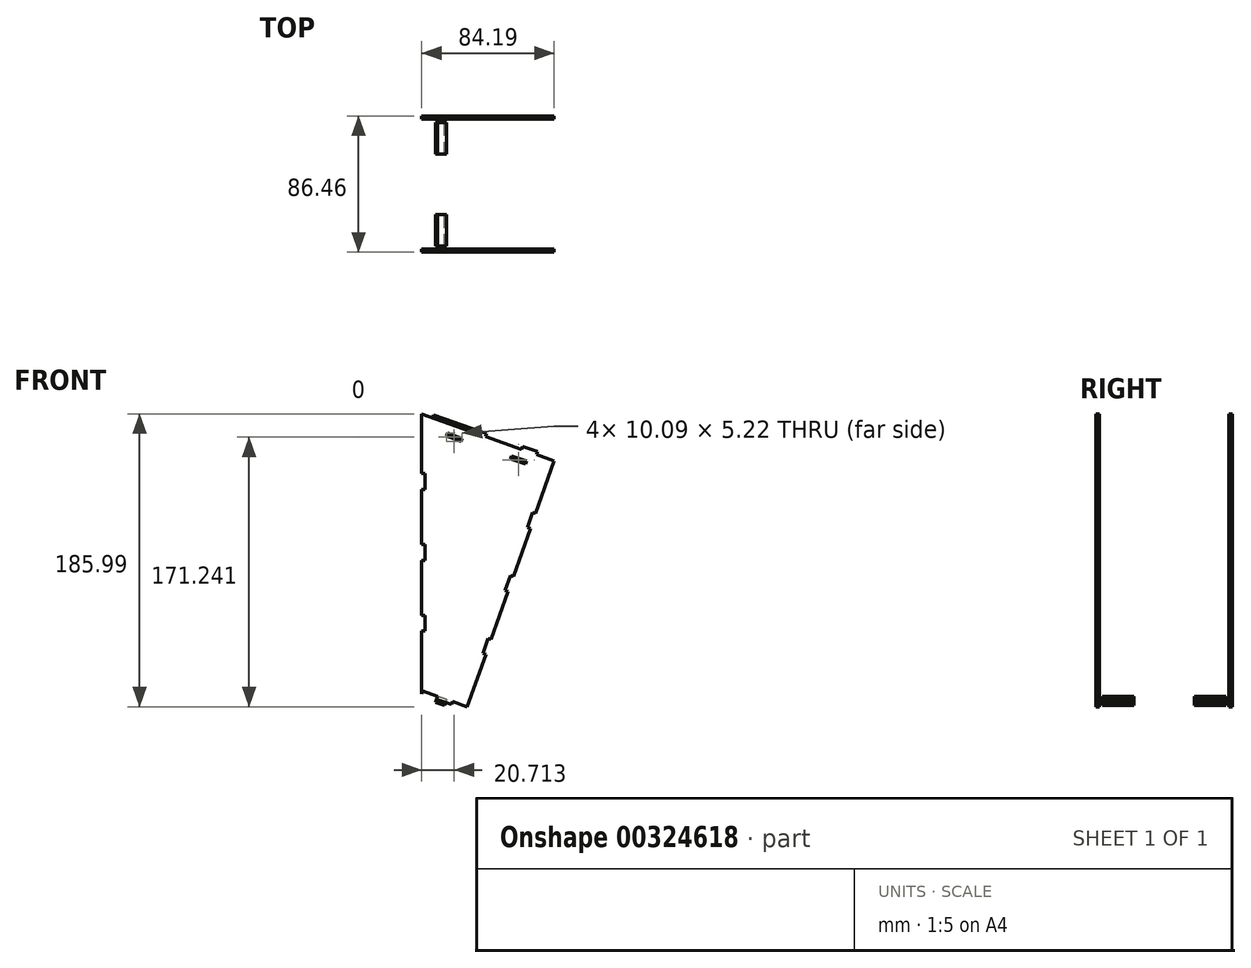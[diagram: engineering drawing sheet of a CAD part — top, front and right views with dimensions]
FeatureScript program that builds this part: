
annotation { "Feature Type Name" : "Feature", "Feature Type Description" : "" }
export const myFeature = defineFeature(function(context is Context, id is Id, definition is map)
    precondition{}
    {
        {
            assignVariable(context, id + "F0", {"name" : "WT", "anyValue" : 2});
        }
        {
            var Q0;
            Q0=qCreatedBy(makeId("Front.planeOp"),FACE);
            var sketch = newSketch(context, id + "F1", { "sketchPlane" : qUnion([Q0])});
            skLineSegment(sketch, "E0", {"start": v(0, 90) * mm, "end": v(0, -90) * mm});
            skLineSegment(sketch, "E1", {"start": v(0, 90) * mm, "end": v(84.85, 60) * mm});
            skLineSegment(sketch, "E2", {"start": v(28.28, -100) * mm, "end": v(0, -90) * mm});
            skLineSegment(sketch, "E3", {"start": v(28.28, -100) * mm, "end": v(84.85, 60) * mm});
            skPoint(sketch, "E4", {"position": v(28.28, 80) * mm});
            skLineSegment(sketch, "E5", {"start": v(14.14, -95) * mm, "end": v(14.14, 85) * mm, "construction": true});
            skLineSegment(sketch, "E6", {"start": v(11.14, -93.94) * mm, "end": v(11.14, -100) * mm});
            skLineSegment(sketch, "E7", {"start": v(11.14, -100) * mm, "end": v(13.14, -100) * mm});
            skLineSegment(sketch, "E8", {"start": v(13.14, -100) * mm, "end": v(13.14, -94.65) * mm});
            skLineSegment(sketch, "E9", {"start": v(15.14, -95.35) * mm, "end": v(15.14, -100) * mm});
            skLineSegment(sketch, "E10", {"start": v(15.14, -100) * mm, "end": v(17.14, -100) * mm});
            skLineSegment(sketch, "E11", {"start": v(17.14, -100) * mm, "end": v(17.14, -96.06) * mm});
            skLineSegment(sketch, "E12", {"start": v(28.28, -100) * mm, "end": v(11.14, -100) * mm, "construction": true});
            skLineSegment(sketch, "E13", {"start": v(11.14, 86.06) * mm, "end": v(11.14, 80) * mm});
            skLineSegment(sketch, "E14", {"start": v(11.14, 80) * mm, "end": v(17.14, 80) * mm});
            skLineSegment(sketch, "E15", {"start": v(17.14, 80) * mm, "end": v(17.14, 83.94) * mm});
            skLineSegment(sketch, "E16", {"start": v(11.14, -93.94) * mm, "end": v(11.14, 80) * mm, "construction": true});
            skLineSegment(sketch, "E17", {"start": v(17.14, -96.06) * mm, "end": v(17.14, 80) * mm, "construction": true});
            skLineSegment(sketch, "E18", {"start": v(0, 79.4) * mm, "end": v(81.52, 50.57) * mm});
            skPoint(sketch, "E19", {"position": v(17.14, 73.33) * mm});
            skSolve(sketch);
        }
        {
            var Q0;
            Q0=qCreatedBy(makeId("Front.planeOp"),FACE);
            var sketch = newSketch(context, id + "F2", { "sketchPlane" : qUnion([Q0])});
            skLineSegment(sketch, "E20.0", {"start": v(0, 90) * mm, "end": v(0, -90) * mm});
            skLineSegment(sketch, "E20.1", {"start": v(0, 90) * mm, "end": v(84.85, 60) * mm});
            skLineSegment(sketch, "E20.2", {"start": v(28.28, -100) * mm, "end": v(84.85, 60) * mm});
            skLineSegment(sketch, "E20.3", {"start": v(28.28, -100) * mm, "end": v(0, -90) * mm});
            skSolve(sketch);
        }
        {
            var Q0;
            Q0=sQuery(id+"F1.wireOp",EDGE,"E18");
            cPlane(context, id + "F3", {"entities" : qUnion([Q0]), "cplaneType" : CPlaneType.LINE_ANGLE, "offset" : 25 * mm, "angle" : 90 * degree, "width" : 150 * mm, "height" : 150 * mm});
        }
        {
            var Q0;
            Q0=qCreatedBy(id+"F3.planeOp",FACE);
            var sketch = newSketch(context, id + "F4", { "sketchPlane" : qUnion([Q0])});
            skLineSegment(sketch, "E21.0", {"start": v(-26.46, 0) * mm, "end": v(60, 0) * mm});
            skLineSegment(sketch, "E22", {"start": v(-26.46, 0) * mm, "end": v(-26.46, -86.46) * mm});
            skLineSegment(sketch, "E23", {"start": v(-26.46, -86.46) * mm, "end": v(60, -86.46) * mm});
            skLineSegment(sketch, "E24", {"start": v(60, -86.46) * mm, "end": v(60, 0) * mm});
            skLineSegment(sketch, "E25.0", {"start": v(48.18, 0) * mm, "end": v(-10.5, 0) * mm, "construction": true});
            skLineSegment(sketch, "E26", {"start": v(-8.28, 0) * mm, "end": v(-8.28, -86.46) * mm, "construction": true});
            skLineSegment(sketch, "E27", {"start": v(-8.28, 0) * mm, "end": v(60, -86.46) * mm, "construction": true});
            skCircle(sketch, "E28", {"center": v(25.86, -43.23) * mm, "radius": 25 * mm});
            skLineSegment(sketch, "E29.0", {"start": v(-24.46, -84.46) * mm, "end": v(62, -84.46) * mm});
            skLineSegment(sketch, "E29.1", {"start": v(-24.46, -2) * mm, "end": v(-24.46, -84.46) * mm});
            skLineSegment(sketch, "E29.2", {"start": v(-24.46, -2) * mm, "end": v(58, -2) * mm});
            skLineSegment(sketch, "E30", {"start": v(-26.46, -43.23) * mm, "end": v(60, -43.23) * mm, "construction": true});
            skLineSegment(sketch, "E31", {"start": v(16.77, -43.23) * mm, "end": v(16.77, 0) * mm, "construction": true});
            skLineSegment(sketch, "E32", {"start": v(16.77, -21.62) * mm, "end": v(-26.46, -21.62) * mm, "construction": true});
            skLineSegment(sketch, "E33", {"start": v(-26.46, -26.62) * mm, "end": v(-24.46, -26.62) * mm});
            skLineSegment(sketch, "E34", {"start": v(-26.46, -16.62) * mm, "end": v(-24.46, -16.62) * mm});
            skLineSegment(sketch, "E35.MirrorCS", {"start": v(-26.46, -59.85) * mm, "end": v(-24.46, -59.85) * mm});
            skLineSegment(sketch, "E36.MirrorCS", {"start": v(-26.46, -69.85) * mm, "end": v(-24.46, -69.85) * mm});
            skLineSegment(sketch, "E37", {"start": v(-4.85, -21.62) * mm, "end": v(-4.85, -86.46) * mm, "construction": true});
            skLineSegment(sketch, "E38", {"start": v(-9.85, -86.46) * mm, "end": v(-9.85, -84.46) * mm});
            skLineSegment(sketch, "E39", {"start": v(0.15, -86.46) * mm, "end": v(0.15, -84.46) * mm});
            skLineSegment(sketch, "E40.MirrorCS", {"start": v(0.15, 0) * mm, "end": v(0.15, -2) * mm});
            skLineSegment(sketch, "E41.MirrorCS", {"start": v(-9.85, 0) * mm, "end": v(-9.85, -2) * mm});
            skLineSegment(sketch, "E42.MirrorCS", {"start": v(33.38, -86.46) * mm, "end": v(33.38, -84.46) * mm});
            skLineSegment(sketch, "E43.MirrorCS", {"start": v(43.38, -86.46) * mm, "end": v(43.38, -84.46) * mm});
            skLineSegment(sketch, "E44.MirrorCS", {"start": v(33.38, 0) * mm, "end": v(33.38, -2) * mm});
            skLineSegment(sketch, "E45.MirrorCS", {"start": v(43.38, 0) * mm, "end": v(43.38, -2) * mm});
            skLineSegment(sketch, "E46.MirrorCS", {"start": v(60, -69.85) * mm, "end": v(58, -69.85) * mm});
            skLineSegment(sketch, "E47.MirrorCS", {"start": v(60, -59.85) * mm, "end": v(58, -59.85) * mm});
            skLineSegment(sketch, "E48.MirrorCS", {"start": v(60, -26.62) * mm, "end": v(58, -26.62) * mm});
            skLineSegment(sketch, "E49.MirrorCS", {"start": v(60, -16.62) * mm, "end": v(58, -16.62) * mm});
            skLineSegment(sketch, "E50", {"start": v(60, -84.46) * mm, "end": v(62, -84.46) * mm});
            skLineSegment(sketch, "E51", {"start": v(58, -2) * mm, "end": v(60, -2) * mm});
            skLineSegment(sketch, "E52", {"start": v(58, 0) * mm, "end": v(58, -86.46) * mm});
            skSolve(sketch);
        }
        {
            var Q0;
            Q0=sQuery(id+"F2.wireOp",EDGE,"E20.1");
            cPlane(context, id + "F5", {"entities" : qUnion([Q0]), "cplaneType" : CPlaneType.LINE_ANGLE, "offset" : 25 * mm, "angle" : 90 * degree, "width" : 150 * mm, "height" : 150 * mm});
        }
        {
            var Q0;
            Q0=qCreatedBy(id+"F5.planeOp",FACE);
            var sketch = newSketch(context, id + "F6", { "sketchPlane" : qUnion([Q0])});
            skLineSegment(sketch, "E53.0", {"start": v(-30, 0) * mm, "end": v(60, 0) * mm});
            skLineSegment(sketch, "E54.0", {"start": v(60, -86.46) * mm, "end": v(60, 0) * mm});
            skLineSegment(sketch, "E55.0", {"start": v(-8.28, 0) * mm, "end": v(60, -86.46) * mm, "construction": true});
            skCircle(sketch, "E56", {"center": v(25.86, -43.23) * mm, "radius": 30 * mm});
            skLineSegment(sketch, "E57", {"start": v(-30, 0) * mm, "end": v(-30, -86.46) * mm});
            skLineSegment(sketch, "E58.0", {"start": v(-18.18, 0) * mm, "end": v(-16.16, 0) * mm});
            skLineSegment(sketch, "E59.0", {"start": v(-10.5, 0) * mm, "end": v(-11.82, 0) * mm});
            skLineSegment(sketch, "E60", {"start": v(-22, 0) * mm, "end": v(-22, -95.78) * mm});
            skLineSegment(sketch, "E61", {"start": v(-12, 0) * mm, "end": v(-12, -95.78) * mm});
            skLineSegment(sketch, "E62", {"start": v(-22, -2) * mm, "end": v(-12, -2) * mm});
            skLineSegment(sketch, "E63", {"start": v(-22, -84.46) * mm, "end": v(-12, -84.46) * mm});
            skLineSegment(sketch, "E64", {"start": v(-30, -86.46) * mm, "end": v(60, -86.46) * mm});
            skLineSegment(sketch, "E65", {"start": v(-12, -84.46) * mm, "end": v(60, -84.46) * mm});
            skLineSegment(sketch, "E66", {"start": v(-22, -84.46) * mm, "end": v(-30, -84.46) * mm});
            skLineSegment(sketch, "E67", {"start": v(-28, -84.46) * mm, "end": v(-28, -2) * mm});
            skLineSegment(sketch, "E68", {"start": v(-22, -2) * mm, "end": v(-30, -2) * mm});
            skLineSegment(sketch, "E69", {"start": v(-12, -2) * mm, "end": v(60, -2) * mm});
            skLineSegment(sketch, "E70", {"start": v(25.86, -43.23) * mm, "end": v(25.86, 0) * mm, "construction": true});
            skLineSegment(sketch, "E71", {"start": v(25.86, 0) * mm, "end": v(60, -2) * mm, "construction": true});
            skLineSegment(sketch, "E72", {"start": v(42.93, -1) * mm, "end": v(42.93, 0) * mm, "construction": true});
            skLineSegment(sketch, "E73", {"start": v(37.93, 0) * mm, "end": v(37.93, -2) * mm});
            skLineSegment(sketch, "E74", {"start": v(47.93, -2) * mm, "end": v(47.93, 0) * mm});
            skLineSegment(sketch, "E75.MirrorCS", {"start": v(13.79, 0) * mm, "end": v(13.79, -2) * mm});
            skLineSegment(sketch, "E76.MirrorCS", {"start": v(3.79, -2) * mm, "end": v(3.79, 0) * mm});
            skLineSegment(sketch, "E77", {"start": v(25.86, -43.23) * mm, "end": v(44.36, -43.23) * mm, "construction": true});
            skLineSegment(sketch, "E78.MirrorCS", {"start": v(3.79, -84.46) * mm, "end": v(3.79, -86.46) * mm});
            skLineSegment(sketch, "E79.MirrorCS", {"start": v(13.79, -86.46) * mm, "end": v(13.79, -84.46) * mm});
            skLineSegment(sketch, "E80.MirrorCS", {"start": v(37.93, -86.46) * mm, "end": v(37.93, -84.46) * mm});
            skLineSegment(sketch, "E81.MirrorCS", {"start": v(47.93, -84.46) * mm, "end": v(47.93, -86.46) * mm});
            skSolve(sketch);
        }
        {
            var Q0;
            Q0=sQuery(id+"F1.wireOp",EDGE,"E1");
            cPlane(context, id + "F7", {"entities" : qUnion([Q0]), "cplaneType" : CPlaneType.LINE_ANGLE, "offset" : 25 * mm, "angle" : 90 * degree, "width" : 150 * mm, "height" : 150 * mm});
        }
        {
            var Q0;
            Q0=qCreatedBy(makeId("Right.planeOp"),FACE);
            var sketch = newSketch(context, id + "F8", { "sketchPlane" : qUnion([Q0])});
            skLineSegment(sketch, "E82.0", {"start": v(0, 90) * mm, "end": v(0, -90) * mm});
            skLineSegment(sketch, "E83", {"start": v(-86.46, 90) * mm, "end": v(-86.46, -90) * mm});
            skLineSegment(sketch, "E84", {"start": v(-86.46, -90) * mm, "end": v(0, -90) * mm});
            skLineSegment(sketch, "E85.0", {"start": v(0, 90) * mm, "end": v(-86.46, 90) * mm});
            skLineSegment(sketch, "E86.0", {"start": v(-2, 88) * mm, "end": v(-2, -88) * mm});
            skLineSegment(sketch, "E86.1", {"start": v(-2, 88) * mm, "end": v(-84.46, 88) * mm});
            skLineSegment(sketch, "E86.2", {"start": v(-84.46, 88) * mm, "end": v(-84.46, -88) * mm});
            skLineSegment(sketch, "E86.3", {"start": v(-84.46, -88) * mm, "end": v(-2, -88) * mm});
            skLineSegment(sketch, "E87", {"start": v(-43.23, 90) * mm, "end": v(-43.23, -90) * mm, "construction": true});
            skLineSegment(sketch, "E88", {"start": v(-86.46, 0) * mm, "end": v(0, 0) * mm, "construction": true});
            skLineSegment(sketch, "E89", {"start": v(-86.46, 90) * mm, "end": v(0, -90) * mm, "construction": true});
            skLineSegment(sketch, "E90", {"start": v(-43.23, 0) * mm, "end": v(-86.46, -90) * mm, "construction": true});
            skLineSegment(sketch, "E91", {"start": v(-64.85, -45) * mm, "end": v(0, -45) * mm, "construction": true});
            skLineSegment(sketch, "E92", {"start": v(0, -40) * mm, "end": v(-2, -40) * mm});
            skLineSegment(sketch, "E93.MirrorCS", {"start": v(0, -50) * mm, "end": v(-2, -50) * mm});
            skLineSegment(sketch, "E94", {"start": v(-21.62, -22.5) * mm, "end": v(0, -22.5) * mm, "construction": true});
            skLineSegment(sketch, "E95.MirrorCS", {"start": v(0, -5) * mm, "end": v(-2, -5) * mm});
            skLineSegment(sketch, "E96.MirrorCS", {"start": v(0, 5) * mm, "end": v(-2, 5) * mm});
            skLineSegment(sketch, "E97", {"start": v(0, -45) * mm, "end": v(-43.23, 0) * mm, "construction": true});
            skLineSegment(sketch, "E98.MirrorCS", {"start": v(0, 40) * mm, "end": v(-2, 40) * mm});
            skLineSegment(sketch, "E99.MirrorCS", {"start": v(0, 50) * mm, "end": v(-2, 50) * mm});
            skLineSegment(sketch, "E100.MirrorCS", {"start": v(-86.46, 50) * mm, "end": v(-84.46, 50) * mm});
            skLineSegment(sketch, "E101.MirrorCS", {"start": v(-86.46, 40) * mm, "end": v(-84.46, 40) * mm});
            skLineSegment(sketch, "E102.MirrorCS", {"start": v(-86.46, 5) * mm, "end": v(-84.46, 5) * mm});
            skLineSegment(sketch, "E103.MirrorCS", {"start": v(-86.46, -5) * mm, "end": v(-84.46, -5) * mm});
            skLineSegment(sketch, "E104.MirrorCS", {"start": v(-86.46, -40) * mm, "end": v(-84.46, -40) * mm});
            skLineSegment(sketch, "E105.MirrorCS", {"start": v(-86.46, -50) * mm, "end": v(-84.46, -50) * mm});
            skLineSegment(sketch, "E106", {"start": v(-21.62, -22.5) * mm, "end": v(-21.62, -90) * mm, "construction": true});
            skLineSegment(sketch, "E107", {"start": v(-16.62, -88) * mm, "end": v(-16.62, -90) * mm});
            skLineSegment(sketch, "E108.MirrorCS", {"start": v(-26.62, -88) * mm, "end": v(-26.62, -90) * mm});
            skLineSegment(sketch, "E109.MirrorCS", {"start": v(-59.85, -88) * mm, "end": v(-59.85, -90) * mm});
            skLineSegment(sketch, "E110.MirrorCS", {"start": v(-69.85, -88) * mm, "end": v(-69.85, -90) * mm});
            skLineSegment(sketch, "E111.MirrorCS", {"start": v(-16.62, 88) * mm, "end": v(-16.62, 90) * mm});
            skLineSegment(sketch, "E112.MirrorCS", {"start": v(-26.62, 88) * mm, "end": v(-26.62, 90) * mm});
            skLineSegment(sketch, "E113.MirrorCS", {"start": v(-59.85, 88) * mm, "end": v(-59.85, 90) * mm});
            skLineSegment(sketch, "E114.MirrorCS", {"start": v(-69.85, 88) * mm, "end": v(-69.85, 90) * mm});
            skSolve(sketch);
        }
        {
            var Q0;
            Q0=sQuery(id+"F1.wireOp",EDGE,"E2");
            cPlane(context, id + "F9", {"entities" : qUnion([Q0]), "cplaneType" : CPlaneType.LINE_ANGLE, "offset" : 25 * mm, "angle" : 90 * degree, "width" : 150 * mm, "height" : 150 * mm});
        }
        {
            var Q0;
            Q0=sQuery(id+"F1.wireOp",EDGE,"E3");
            cPlane(context, id + "F10", {"entities" : qUnion([Q0]), "cplaneType" : CPlaneType.LINE_ANGLE, "offset" : 25 * mm, "angle" : 0 * degree, "width" : 150 * mm, "height" : 150 * mm});
        }
        {
            var Q0;
            Q0=qCreatedBy(id+"F10.planeOp",FACE);
            var sketch = newSketch(context, id + "F11", { "sketchPlane" : qUnion([Q0])});
            skLineSegment(sketch, "E115.0", {"start": v(0, -84.85) * mm, "end": v(0, 84.85) * mm});
            skLineSegment(sketch, "E116.0", {"start": v(-86.46, 84.85) * mm, "end": v(0, 84.85) * mm});
            skLineSegment(sketch, "E117", {"start": v(-86.46, 84.85) * mm, "end": v(-86.46, -84.85) * mm});
            skLineSegment(sketch, "E118", {"start": v(-86.46, -84.85) * mm, "end": v(0, -84.85) * mm});
            skLineSegment(sketch, "E119.0", {"start": v(-84.46, 82.85) * mm, "end": v(-84.46, -82.85) * mm});
            skLineSegment(sketch, "E119.1", {"start": v(-84.46, 82.85) * mm, "end": v(-2, 82.85) * mm});
            skLineSegment(sketch, "E119.2", {"start": v(-2, -82.85) * mm, "end": v(-2, 82.85) * mm});
            skLineSegment(sketch, "E119.3", {"start": v(-84.46, -82.85) * mm, "end": v(-2, -82.85) * mm});
            skLineSegment(sketch, "E120", {"start": v(-43.23, 84.85) * mm, "end": v(-43.23, -84.85) * mm, "construction": true});
            skLineSegment(sketch, "E121", {"start": v(0, 0) * mm, "end": v(-86.46, 0) * mm, "construction": true});
            skLineSegment(sketch, "E122", {"start": v(-86.46, 0) * mm, "end": v(-43.23, 84.85) * mm, "construction": true});
            skLineSegment(sketch, "E123", {"start": v(-64.85, 42.43) * mm, "end": v(-64.85, 84.85) * mm, "construction": true});
            skLineSegment(sketch, "E124", {"start": v(-69.85, 82.85) * mm, "end": v(-69.85, 84.85) * mm});
            skLineSegment(sketch, "E125", {"start": v(-59.85, 82.85) * mm, "end": v(-59.85, 84.85) * mm});
            skLineSegment(sketch, "E126.MirrorCS", {"start": v(-16.62, 82.85) * mm, "end": v(-16.62, 84.85) * mm});
            skLineSegment(sketch, "E127.MirrorCS", {"start": v(-26.62, 82.85) * mm, "end": v(-26.62, 84.85) * mm});
            skLineSegment(sketch, "E128.MirrorCS", {"start": v(-69.85, -82.85) * mm, "end": v(-69.85, -84.85) * mm});
            skLineSegment(sketch, "E129.MirrorCS", {"start": v(-59.85, -82.85) * mm, "end": v(-59.85, -84.85) * mm});
            skLineSegment(sketch, "E130.MirrorCS", {"start": v(-26.62, -82.85) * mm, "end": v(-26.62, -84.85) * mm});
            skLineSegment(sketch, "E131.MirrorCS", {"start": v(-16.62, -82.85) * mm, "end": v(-16.62, -84.85) * mm});
            skLineSegment(sketch, "E132", {"start": v(-86.46, 5) * mm, "end": v(-84.46, 5) * mm});
            skLineSegment(sketch, "E133", {"start": v(-86.46, -5) * mm, "end": v(-84.46, -5) * mm});
            skLineSegment(sketch, "E134", {"start": v(-64.85, 42.43) * mm, "end": v(-86.46, 42.43) * mm, "construction": true});
            skLineSegment(sketch, "E135", {"start": v(-86.46, 47.43) * mm, "end": v(-84.46, 47.43) * mm});
            skLineSegment(sketch, "E136", {"start": v(-86.46, 37.43) * mm, "end": v(-84.46, 37.43) * mm});
            skLineSegment(sketch, "E137.MirrorCS", {"start": v(0, 47.43) * mm, "end": v(-2, 47.43) * mm});
            skLineSegment(sketch, "E138.MirrorCS", {"start": v(0, 37.43) * mm, "end": v(-2, 37.43) * mm});
            skLineSegment(sketch, "E139.MirrorCS", {"start": v(0, 5) * mm, "end": v(-2, 5) * mm});
            skLineSegment(sketch, "E140.MirrorCS", {"start": v(0, -5) * mm, "end": v(-2, -5) * mm});
            skLineSegment(sketch, "E141.MirrorCS", {"start": v(-86.46, -37.43) * mm, "end": v(-84.46, -37.43) * mm});
            skLineSegment(sketch, "E142.MirrorCS", {"start": v(-86.46, -47.43) * mm, "end": v(-84.46, -47.43) * mm});
            skLineSegment(sketch, "E143.MirrorCS", {"start": v(0, -37.43) * mm, "end": v(-2, -37.43) * mm});
            skLineSegment(sketch, "E144.MirrorCS", {"start": v(0, -47.43) * mm, "end": v(-2, -47.43) * mm});
            skSolve(sketch);
        }
        {
            var Q0;
            Q0=sQuery(id+"F11.wireOp",EDGE,"E117");
            cPlane(context, id + "F12", {"entities" : qUnion([Q0]), "cplaneType" : CPlaneType.LINE_ANGLE, "offset" : 25 * mm, "angle" : 90 * degree, "width" : 150 * mm, "height" : 150 * mm});
        }
        {
            var Q0;
            Q0=qCreatedBy(id+"F12.planeOp",FACE);
            var sketch = newSketch(context, id + "F13", { "sketchPlane" : qUnion([Q0])});
            skLineSegment(sketch, "E145.0", {"start": v(0, 90) * mm, "end": v(0, -90) * mm});
            skLineSegment(sketch, "E145.1", {"start": v(-28.28, -100) * mm, "end": v(0, -90) * mm});
            skLineSegment(sketch, "E145.2", {"start": v(-28.28, -100) * mm, "end": v(-84.85, 60) * mm});
            skLineSegment(sketch, "E145.3", {"start": v(0, 90) * mm, "end": v(-84.85, 60) * mm});
            skSolve(sketch);
        }
        {
            var Q0;
            Q0=qCreatedBy(id+"F9.planeOp",FACE);
            var sketch = newSketch(context, id + "F14", { "sketchPlane" : qUnion([Q0])});
            skLineSegment(sketch, "E146.0", {"start": v(60, -86.46) * mm, "end": v(60, 0) * mm});
            skLineSegment(sketch, "E147.0", {"start": v(60, -86.46) * mm, "end": v(30, -86.46) * mm});
            skLineSegment(sketch, "E148", {"start": v(30, -86.46) * mm, "end": v(30, 0) * mm});
            skLineSegment(sketch, "E149", {"start": v(30, 0) * mm, "end": v(60, 0) * mm});
            skLineSegment(sketch, "E150.0", {"start": v(32, -84.46) * mm, "end": v(32, -2) * mm});
            skLineSegment(sketch, "E150.1", {"start": v(58, -84.46) * mm, "end": v(32, -84.46) * mm});
            skLineSegment(sketch, "E150.2", {"start": v(58, -84.46) * mm, "end": v(58, -2) * mm});
            skLineSegment(sketch, "E150.3", {"start": v(32, -2) * mm, "end": v(58, -2) * mm});
            skLineSegment(sketch, "E151", {"start": v(58, -84.46) * mm, "end": v(32, -2) * mm, "construction": true});
            skLineSegment(sketch, "E152", {"start": v(45, -43.23) * mm, "end": v(32, -43.23) * mm, "construction": true});
            skLineSegment(sketch, "E153.bottom", {"start": v(48, -84.46) * mm, "end": v(38, -84.46) * mm});
            skLineSegment(sketch, "E153.top", {"start": v(48, -2) * mm, "end": v(38, -2) * mm});
            skLineSegment(sketch, "E153.left", {"start": v(48, -84.46) * mm, "end": v(48, -2) * mm});
            skLineSegment(sketch, "E153.right", {"start": v(38, -84.46) * mm, "end": v(38, -2) * mm});
            skPoint(sketch, "E153.middle", {"position": v(43, -43.23) * mm});
            skLineSegment(sketch, "E154.0", {"start": v(46, -82.46) * mm, "end": v(46, -4) * mm});
            skLineSegment(sketch, "E154.1", {"start": v(46, -82.46) * mm, "end": v(40, -82.46) * mm});
            skLineSegment(sketch, "E154.2", {"start": v(40, -82.46) * mm, "end": v(40, -4) * mm});
            skLineSegment(sketch, "E154.3", {"start": v(46, -4) * mm, "end": v(40, -4) * mm});
            skLineSegment(sketch, "E155", {"start": v(45, 0) * mm, "end": v(45, -2) * mm, "construction": true});
            skLineSegment(sketch, "E156", {"start": v(40, 0) * mm, "end": v(40, -2) * mm});
            skLineSegment(sketch, "E157.MirrorCS", {"start": v(50, 0) * mm, "end": v(50, -2) * mm});
            skLineSegment(sketch, "E158.MirrorCS", {"start": v(40, -86.46) * mm, "end": v(40, -84.46) * mm});
            skLineSegment(sketch, "E159.MirrorCS", {"start": v(50, -86.46) * mm, "end": v(50, -84.46) * mm});
            skLineSegment(sketch, "E160", {"start": v(40, -24) * mm, "end": v(46, -24) * mm});
            skLineSegment(sketch, "E161.MirrorCS", {"start": v(40, -62.46) * mm, "end": v(46, -62.46) * mm});
            skSolve(sketch);
        }
        {
            var Q0;
            Q0=makeQuery(id+"F2.imprint","IMPRINT",FACE,{"disambiguationData":[TD([[makeQuery(id+"F2.imprint","IMPRINT",EDGE,{"derivedFrom":sQuery(id+"F2.wireOp",EDGE,"E20.0")}),1.0]])]});
            extrude(context, id + "F15", {"entities" : qUnion([Q0]), "depth" : (getVariable(context, 'WT')) * mm});
        }
        {
            var Q0;
            {var subQ12=sQuery(id+"F8.wireOp",EDGE,"E86.1");var subQ16=sQuery(id+"F8.wireOp",EDGE,"E86.0");var subQ21=makeQuery(id+"F8.imprint","INTERSECT",VERTEX,{"derivedFrom":[subQ16,subQ12]});Q0=makeQuery(id+"F8.imprint","IMPRINT",FACE,{"disambiguationData":[TD([[makeQuery(id+"F8.imprint","IMPRINT",EDGE,{"disambiguationData":[TD([[subQ21,-1.0]])],"derivedFrom":subQ16}),-1.0]])]});}
            var Q1;
            {var subQ0=sQuery(id+"F8.wireOp",EDGE,"E98.MirrorCS");Q1=makeQuery(id+"F8.imprint","IMPRINT",FACE,{"disambiguationData":[TD([[makeQuery(id+"F8.imprint","IMPRINT",EDGE,{"derivedFrom":subQ0}),-1.0]])]});}
            var Q2;
            {var subQ0=sQuery(id+"F8.wireOp",EDGE,"E100.MirrorCS");Q2=makeQuery(id+"F8.imprint","IMPRINT",FACE,{"disambiguationData":[TD([[makeQuery(id+"F8.imprint","IMPRINT",EDGE,{"derivedFrom":subQ0}),-1.0]])]});}
            var Q3;
            {var subQ0=sQuery(id+"F8.wireOp",EDGE,"E102.MirrorCS");Q3=makeQuery(id+"F8.imprint","IMPRINT",FACE,{"disambiguationData":[TD([[makeQuery(id+"F8.imprint","IMPRINT",EDGE,{"derivedFrom":subQ0}),-1.0]])]});}
            var Q4;
            {var subQ0=sQuery(id+"F8.wireOp",EDGE,"E104.MirrorCS");Q4=makeQuery(id+"F8.imprint","IMPRINT",FACE,{"disambiguationData":[TD([[makeQuery(id+"F8.imprint","IMPRINT",EDGE,{"derivedFrom":subQ0}),-1.0]])]});}
            var Q5;
            {var subQ0=sQuery(id+"F8.wireOp",EDGE,"E109.MirrorCS");Q5=makeQuery(id+"F8.imprint","IMPRINT",FACE,{"disambiguationData":[TD([[makeQuery(id+"F8.imprint","IMPRINT",EDGE,{"derivedFrom":subQ0}),-1.0]])]});}
            var Q6;
            {var subQ0=sQuery(id+"F8.wireOp",EDGE,"E107");Q6=makeQuery(id+"F8.imprint","IMPRINT",FACE,{"disambiguationData":[TD([[makeQuery(id+"F8.imprint","IMPRINT",EDGE,{"derivedFrom":subQ0}),-1.0]])]});}
            var Q7;
            {var subQ0=sQuery(id+"F8.wireOp",EDGE,"E92");Q7=makeQuery(id+"F8.imprint","IMPRINT",FACE,{"disambiguationData":[TD([[makeQuery(id+"F8.imprint","IMPRINT",EDGE,{"derivedFrom":subQ0}),1.0]])]});}
            var Q8;
            {var subQ0=sQuery(id+"F8.wireOp",EDGE,"E95.MirrorCS");Q8=makeQuery(id+"F8.imprint","IMPRINT",FACE,{"disambiguationData":[TD([[makeQuery(id+"F8.imprint","IMPRINT",EDGE,{"derivedFrom":subQ0}),-1.0]])]});}
            extrude(context, id + "F16", {"entities" : qUnion([Q0, Q1, Q2, Q3, Q4, Q5, Q6, Q7, Q8]), "depth" : (getVariable(context, 'WT')) * mm});
        }
        {
            var Q0;
            {var subQ4=sQuery(id+"F11.wireOp",EDGE,"E119.0");var subQ7=sQuery(id+"F11.wireOp",EDGE,"E119.1");var subQ22=makeQuery(id+"F11.imprint","INTERSECT",VERTEX,{"derivedFrom":[subQ4,subQ7]});Q0=makeQuery(id+"F11.imprint","IMPRINT",FACE,{"disambiguationData":[TD([[makeQuery(id+"F11.imprint","IMPRINT",EDGE,{"disambiguationData":[TD([[subQ22,-1.0]])],"derivedFrom":subQ4}),1.0]])]});}
            var Q1;
            {var subQ0=sQuery(id+"F11.wireOp",EDGE,"E132");Q1=makeQuery(id+"F11.imprint","IMPRINT",FACE,{"disambiguationData":[TD([[makeQuery(id+"F11.imprint","IMPRINT",EDGE,{"derivedFrom":subQ0}),-1.0]])]});}
            var Q2;
            {var subQ0=sQuery(id+"F11.wireOp",EDGE,"E135");Q2=makeQuery(id+"F11.imprint","IMPRINT",FACE,{"disambiguationData":[TD([[makeQuery(id+"F11.imprint","IMPRINT",EDGE,{"derivedFrom":subQ0}),-1.0]])]});}
            var Q3;
            {var subQ0=sQuery(id+"F11.wireOp",EDGE,"E141.MirrorCS");Q3=makeQuery(id+"F11.imprint","IMPRINT",FACE,{"disambiguationData":[TD([[makeQuery(id+"F11.imprint","IMPRINT",EDGE,{"derivedFrom":subQ0}),-1.0]])]});}
            var Q4;
            {var subQ0=sQuery(id+"F11.wireOp",EDGE,"E128.MirrorCS");Q4=makeQuery(id+"F11.imprint","IMPRINT",FACE,{"disambiguationData":[TD([[makeQuery(id+"F11.imprint","IMPRINT",EDGE,{"derivedFrom":subQ0}),1.0]])]});}
            var Q5;
            {var subQ0=sQuery(id+"F11.wireOp",EDGE,"E130.MirrorCS");Q5=makeQuery(id+"F11.imprint","IMPRINT",FACE,{"disambiguationData":[TD([[makeQuery(id+"F11.imprint","IMPRINT",EDGE,{"derivedFrom":subQ0}),1.0]])]});}
            var Q6;
            {var subQ0=sQuery(id+"F11.wireOp",EDGE,"E143.MirrorCS");Q6=makeQuery(id+"F11.imprint","IMPRINT",FACE,{"disambiguationData":[TD([[makeQuery(id+"F11.imprint","IMPRINT",EDGE,{"derivedFrom":subQ0}),1.0]])]});}
            var Q7;
            {var subQ0=sQuery(id+"F11.wireOp",EDGE,"E139.MirrorCS");Q7=makeQuery(id+"F11.imprint","IMPRINT",FACE,{"disambiguationData":[TD([[makeQuery(id+"F11.imprint","IMPRINT",EDGE,{"derivedFrom":subQ0}),1.0]])]});}
            var Q8;
            {var subQ0=sQuery(id+"F11.wireOp",EDGE,"E137.MirrorCS");Q8=makeQuery(id+"F11.imprint","IMPRINT",FACE,{"disambiguationData":[TD([[makeQuery(id+"F11.imprint","IMPRINT",EDGE,{"derivedFrom":subQ0}),1.0]])]});}
            var Q9;
            {var subQ0=sQuery(id+"F11.wireOp",EDGE,"E126.MirrorCS");Q9=makeQuery(id+"F11.imprint","IMPRINT",FACE,{"disambiguationData":[TD([[makeQuery(id+"F11.imprint","IMPRINT",EDGE,{"derivedFrom":subQ0}),1.0]])]});}
            var Q10;
            {var subQ0=sQuery(id+"F11.wireOp",EDGE,"E124");Q10=makeQuery(id+"F11.imprint","IMPRINT",FACE,{"disambiguationData":[TD([[makeQuery(id+"F11.imprint","IMPRINT",EDGE,{"derivedFrom":subQ0}),-1.0]])]});}
            extrude(context, id + "F17", {"entities" : qUnion([Q0, Q1, Q2, Q3, Q4, Q5, Q6, Q7, Q8, Q9, Q10]), "oppositeDirection" : true, "depth" : (getVariable(context, 'WT')) * mm});
        }
        {
            var Q0;
            Q0=makeQuery(id+"F6.imprint","IMPRINT",FACE,{"disambiguationData":[TD([[makeQuery(id+"F6.imprint","IMPRINT",EDGE,{"derivedFrom":sQuery(id+"F6.wireOp",EDGE,"E56")}),-1.0]])]});
            var Q1;
            {var subQ5=sQuery(id+"F6.wireOp",EDGE,"E67");Q1=makeQuery(id+"F6.imprint","IMPRINT",FACE,{"disambiguationData":[TD([[makeQuery(id+"F6.imprint","IMPRINT",EDGE,{"derivedFrom":subQ5}),1.0]])]});}
            var Q2;
            {var subQ4=sQuery(id+"F6.wireOp",EDGE,"E64");var subQ5=sQuery(id+"F6.wireOp",EDGE,"E57");var subQ6=makeQuery(id+"F6.imprint","INTERSECT",VERTEX,{"derivedFrom":[subQ5,subQ4]});Q2=makeQuery(id+"F6.imprint","IMPRINT",FACE,{"disambiguationData":[TD([[makeQuery(id+"F6.imprint","IMPRINT",EDGE,{"disambiguationData":[TD([[subQ6,1.0]])],"derivedFrom":subQ5}),1.0]])]});}
            var Q3;
            {var subQ3=sQuery(id+"F6.wireOp",EDGE,"E63");Q3=makeQuery(id+"F6.imprint","IMPRINT",FACE,{"disambiguationData":[TD([[makeQuery(id+"F6.imprint","IMPRINT",EDGE,{"derivedFrom":subQ3}),-1.0]])]});}
            var Q4;
            {var subQ5=sQuery(id+"F6.wireOp",EDGE,"E78.MirrorCS");Q4=makeQuery(id+"F6.imprint","IMPRINT",FACE,{"disambiguationData":[TD([[makeQuery(id+"F6.imprint","IMPRINT",EDGE,{"derivedFrom":subQ5}),-1.0]])]});}
            var Q5;
            {var subQ0=sQuery(id+"F6.wireOp",EDGE,"E79.MirrorCS");Q5=makeQuery(id+"F6.imprint","IMPRINT",FACE,{"disambiguationData":[TD([[makeQuery(id+"F6.imprint","IMPRINT",EDGE,{"derivedFrom":subQ0}),-1.0]])]});}
            var Q6;
            {var subQ5=sQuery(id+"F6.wireOp",EDGE,"E81.MirrorCS");Q6=makeQuery(id+"F6.imprint","IMPRINT",FACE,{"disambiguationData":[TD([[makeQuery(id+"F6.imprint","IMPRINT",EDGE,{"derivedFrom":subQ5}),1.0]])]});}
            var Q7;
            {var subQ0=sQuery(id+"F6.wireOp",EDGE,"2n5WLC9Z-0obv-Y2U2-hiql-T8fxuz6A8fkv");Q7=makeQuery(id+"F6.imprint","IMPRINT",FACE,{"disambiguationData":[TD([[makeQuery(id+"F6.imprint","IMPRINT",EDGE,{"derivedFrom":subQ0}),-1.0]])]});}
            var Q8;
            {var subQ3=sQuery(id+"F6.wireOp",EDGE,"E74");Q8=makeQuery(id+"F6.imprint","IMPRINT",FACE,{"disambiguationData":[TD([[makeQuery(id+"F6.imprint","IMPRINT",EDGE,{"derivedFrom":subQ3}),-1.0]])]});}
            var Q9;
            {var subQ0=sQuery(id+"F6.wireOp",EDGE,"E73");Q9=makeQuery(id+"F6.imprint","IMPRINT",FACE,{"disambiguationData":[TD([[makeQuery(id+"F6.imprint","IMPRINT",EDGE,{"derivedFrom":subQ0}),-1.0]])]});}
            var Q10;
            {var subQ6=sQuery(id+"F6.wireOp",EDGE,"E59.0");Q10=makeQuery(id+"F6.imprint","IMPRINT",FACE,{"disambiguationData":[TD([[makeQuery(id+"F6.imprint","IMPRINT",EDGE,{"derivedFrom":subQ6}),1.0]])]});}
            var Q11;
            {var subQ4=sQuery(id+"F6.wireOp",EDGE,"E58.0");Q11=makeQuery(id+"F6.imprint","IMPRINT",FACE,{"disambiguationData":[TD([[makeQuery(id+"F6.imprint","IMPRINT",EDGE,{"derivedFrom":subQ4}),-1.0]])]});}
            var Q12;
            {var subQ4=sQuery(id+"F6.wireOp",EDGE,"E57");var subQ5=sQuery(id+"F6.wireOp",EDGE,"E53.0");var subQ6=makeQuery(id+"F6.imprint","INTERSECT",VERTEX,{"derivedFrom":[subQ5,subQ4]});Q12=makeQuery(id+"F6.imprint","IMPRINT",FACE,{"disambiguationData":[TD([[makeQuery(id+"F6.imprint","IMPRINT",EDGE,{"disambiguationData":[TD([[subQ6,-1.0]])],"derivedFrom":subQ5}),-1.0]])]});}
            var Q13;
            {var subQ5=sQuery(id+"F6.wireOp",EDGE,"E67");Q13=makeQuery(id+"F6.imprint","IMPRINT",FACE,{"disambiguationData":[TD([[makeQuery(id+"F6.imprint","IMPRINT",EDGE,{"derivedFrom":subQ5}),-1.0]])]});}
            extrude(context, id + "F18", {"entities" : qUnion([Q0, Q1, Q2, Q3, Q4, Q5, Q6, Q7, Q8, Q9, Q10, Q11, Q12, Q13]), "oppositeDirection" : true, "depth" : (getVariable(context, 'WT')) * mm});
        }
        {
            var Q0;
            Q0=makeQuery(id+"F4.imprint","IMPRINT",FACE,{"disambiguationData":[TD([[makeQuery(id+"F4.imprint","IMPRINT",EDGE,{"derivedFrom":sQuery(id+"F4.wireOp",EDGE,"E28")}),-1.0]])]});
            var Q1;
            {var subQ0=sQuery(id+"F4.wireOp",EDGE,"rY6iPSDp-yrdz-WOSY-4340-YJhwj86PUc9Y");Q1=makeQuery(id+"F4.imprint","IMPRINT",FACE,{"disambiguationData":[TD([[makeQuery(id+"F4.imprint","IMPRINT",EDGE,{"derivedFrom":subQ0}),1.0]])]});}
            var Q2;
            {var subQ0=sQuery(id+"F4.wireOp",EDGE,"zsETLSQ8-OfV7-wZRS-Cx58-Bi4eRkI4em62");Q2=makeQuery(id+"F4.imprint","IMPRINT",FACE,{"disambiguationData":[TD([[makeQuery(id+"F4.imprint","IMPRINT",EDGE,{"derivedFrom":subQ0}),1.0]])]});}
            var Q3;
            {var subQ0=sQuery(id+"F4.wireOp",EDGE,"E42.MirrorCS");Q3=makeQuery(id+"F4.imprint","IMPRINT",FACE,{"disambiguationData":[TD([[makeQuery(id+"F4.imprint","IMPRINT",EDGE,{"derivedFrom":subQ0}),-1.0]])]});}
            var Q4;
            {var subQ0=sQuery(id+"F4.wireOp",EDGE,"E38");Q4=makeQuery(id+"F4.imprint","IMPRINT",FACE,{"disambiguationData":[TD([[makeQuery(id+"F4.imprint","IMPRINT",EDGE,{"derivedFrom":subQ0}),-1.0]])]});}
            var Q5;
            {var subQ0=sQuery(id+"F4.wireOp",EDGE,"E40.MirrorCS");Q5=makeQuery(id+"F4.imprint","IMPRINT",FACE,{"disambiguationData":[TD([[makeQuery(id+"F4.imprint","IMPRINT",EDGE,{"derivedFrom":subQ0}),-1.0]])]});}
            var Q6;
            {var subQ0=sQuery(id+"F4.wireOp",EDGE,"E44.MirrorCS");Q6=makeQuery(id+"F4.imprint","IMPRINT",FACE,{"disambiguationData":[TD([[makeQuery(id+"F4.imprint","IMPRINT",EDGE,{"derivedFrom":subQ0}),1.0]])]});}
            extrude(context, id + "F19", {"entities" : qUnion([Q0, Q1, Q2, Q3, Q4, Q5, Q6]), "depth" : (getVariable(context, 'WT')) * mm});
        }
        {
            var Q0;
            Q0=makeQuery(id+"F13.imprint","IMPRINT",FACE,{"disambiguationData":[TD([[makeQuery(id+"F13.imprint","IMPRINT",EDGE,{"derivedFrom":sQuery(id+"F13.wireOp",EDGE,"E145.0")}),-1.0]])]});
            extrude(context, id + "F20", {"entities" : qUnion([Q0]), "depth" : (getVariable(context, 'WT')) * mm});
        }
        {
            var Q0;
            Q0=makeQuery(id+"F14.imprint","IMPRINT",FACE,{"disambiguationData":[TD([[makeQuery(id+"F14.imprint","IMPRINT",EDGE,{"derivedFrom":sQuery(id+"F14.wireOp",EDGE,"E150.0")}),-1.0]])]});
            var Q1;
            Q1=makeQuery(id+"F14.imprint","IMPRINT",FACE,{"disambiguationData":[TD([[makeQuery(id+"F14.imprint","IMPRINT",EDGE,{"derivedFrom":sQuery(id+"F14.wireOp",EDGE,"E153.bottom")}),-1.0]])]});
            var Q2;
            {var subQ0=sQuery(id+"F14.wireOp",EDGE,"E150.2");Q2=makeQuery(id+"F14.imprint","IMPRINT",FACE,{"disambiguationData":[TD([[makeQuery(id+"F14.imprint","IMPRINT",EDGE,{"derivedFrom":subQ0}),1.0]])]});}
            var Q3;
            {var subQ4=sQuery(id+"F14.wireOp",EDGE,"E146.0");Q3=makeQuery(id+"F14.imprint","IMPRINT",FACE,{"disambiguationData":[TD([[makeQuery(id+"F14.imprint","IMPRINT",EDGE,{"derivedFrom":subQ4}),1.0]])]});}
            var Q4;
            {var subQ1=sQuery(id+"F14.wireOp",EDGE,"E148");Q4=makeQuery(id+"F14.imprint","IMPRINT",FACE,{"disambiguationData":[TD([[makeQuery(id+"F14.imprint","IMPRINT",EDGE,{"derivedFrom":subQ1}),-1.0]])]});}
            var Q5;
            {var subQ0=sQuery(id+"F14.wireOp",EDGE,"E154.3");Q5=makeQuery(id+"F14.imprint","IMPRINT",FACE,{"disambiguationData":[TD([[makeQuery(id+"F14.imprint","IMPRINT",EDGE,{"derivedFrom":subQ0}),1.0]])]});}
            var Q6;
            {var subQ0=sQuery(id+"F14.wireOp",EDGE,"E154.1");Q6=makeQuery(id+"F14.imprint","IMPRINT",FACE,{"disambiguationData":[TD([[makeQuery(id+"F14.imprint","IMPRINT",EDGE,{"derivedFrom":subQ0}),-1.0]])]});}
            extrude(context, id + "F21", {"entities" : qUnion([Q0, Q1, Q2, Q3, Q4, Q5, Q6]), "depth" : (getVariable(context, 'WT')) * mm});
        }
        {
            var Q0;
            Q0=makeQuery(id+"F14.imprint","IMPRINT",FACE,{"disambiguationData":[TD([[makeQuery(id+"F14.imprint","IMPRINT",EDGE,{"derivedFrom":sQuery(id+"F14.wireOp",EDGE,"E153.bottom")}),-1.0]])]});
            var Q1;
            {var subQ0=sQuery(id+"F14.wireOp",EDGE,"E154.3");Q1=makeQuery(id+"F14.imprint","IMPRINT",FACE,{"disambiguationData":[TD([[makeQuery(id+"F14.imprint","IMPRINT",EDGE,{"derivedFrom":subQ0}),1.0]])]});}
            var Q2;
            {var subQ0=sQuery(id+"F14.wireOp",EDGE,"E154.1");Q2=makeQuery(id+"F14.imprint","IMPRINT",FACE,{"disambiguationData":[TD([[makeQuery(id+"F14.imprint","IMPRINT",EDGE,{"derivedFrom":subQ0}),-1.0]])]});}
            extrude(context, id + "F22", {"entities" : qUnion([Q0, Q1, Q2]), "oppositeDirection" : true, "depth" : (getVariable(context, 'WT')) * mm});
        }
        {
            var Q0;
            Q0=makeQuery(id+"F17.opExtrude","CAP_FACE",FACE,{"disambiguationData":[OSD([sQuery(id+"F11.wireOp",EDGE,"E115.0"),sQuery(id+"F11.wireOp",EDGE,"E116.0"),sQuery(id+"F11.wireOp",EDGE,"E117"),sQuery(id+"F11.wireOp",EDGE,"E118"),sQuery(id+"F11.wireOp",EDGE,"E119.0"),sQuery(id+"F11.wireOp",EDGE,"E119.1"),sQuery(id+"F11.wireOp",EDGE,"E119.2"),sQuery(id+"F11.wireOp",EDGE,"E119.3"),sQuery(id+"F11.wireOp",EDGE,"E124"),sQuery(id+"F11.wireOp",EDGE,"E125"),sQuery(id+"F11.wireOp",EDGE,"E126.MirrorCS"),sQuery(id+"F11.wireOp",EDGE,"E127.MirrorCS"),sQuery(id+"F11.wireOp",EDGE,"E128.MirrorCS"),sQuery(id+"F11.wireOp",EDGE,"E129.MirrorCS"),sQuery(id+"F11.wireOp",EDGE,"E130.MirrorCS"),sQuery(id+"F11.wireOp",EDGE,"E131.MirrorCS"),sQuery(id+"F11.wireOp",EDGE,"E132"),sQuery(id+"F11.wireOp",EDGE,"E133"),sQuery(id+"F11.wireOp",EDGE,"E135"),sQuery(id+"F11.wireOp",EDGE,"E136"),sQuery(id+"F11.wireOp",EDGE,"E137.MirrorCS"),sQuery(id+"F11.wireOp",EDGE,"E138.MirrorCS"),sQuery(id+"F11.wireOp",EDGE,"E139.MirrorCS"),sQuery(id+"F11.wireOp",EDGE,"E140.MirrorCS"),sQuery(id+"F11.wireOp",EDGE,"E141.MirrorCS"),sQuery(id+"F11.wireOp",EDGE,"E142.MirrorCS"),sQuery(id+"F11.wireOp",EDGE,"E143.MirrorCS"),sQuery(id+"F11.wireOp",EDGE,"E144.MirrorCS")])],"isStart":true});
            extrude(context, id + "F23", {"entities" : qUnion([Q0]), "operationType" : NewBodyOperationType.REMOVE, "oppositeDirection" : true, "depth" : (getVariable(context, 'WT')) * mm});
        }
        {
            var Q0;
            Q0=makeQuery(id+"F16.opExtrude","CAP_FACE",FACE,{"disambiguationData":[OSD([sQuery(id+"F8.wireOp",EDGE,"E82.0"),sQuery(id+"F8.wireOp",EDGE,"E83"),sQuery(id+"F8.wireOp",EDGE,"E84"),sQuery(id+"F8.wireOp",EDGE,"E85.0"),sQuery(id+"F8.wireOp",EDGE,"E86.0"),sQuery(id+"F8.wireOp",EDGE,"E86.1"),sQuery(id+"F8.wireOp",EDGE,"E86.2"),sQuery(id+"F8.wireOp",EDGE,"E86.3"),sQuery(id+"F8.wireOp",EDGE,"E92"),sQuery(id+"F8.wireOp",EDGE,"E93.MirrorCS"),sQuery(id+"F8.wireOp",EDGE,"E95.MirrorCS"),sQuery(id+"F8.wireOp",EDGE,"E96.MirrorCS"),sQuery(id+"F8.wireOp",EDGE,"E98.MirrorCS"),sQuery(id+"F8.wireOp",EDGE,"E99.MirrorCS"),sQuery(id+"F8.wireOp",EDGE,"E100.MirrorCS"),sQuery(id+"F8.wireOp",EDGE,"E101.MirrorCS"),sQuery(id+"F8.wireOp",EDGE,"E102.MirrorCS"),sQuery(id+"F8.wireOp",EDGE,"E103.MirrorCS"),sQuery(id+"F8.wireOp",EDGE,"E104.MirrorCS"),sQuery(id+"F8.wireOp",EDGE,"E105.MirrorCS"),sQuery(id+"F8.wireOp",EDGE,"E107"),sQuery(id+"F8.wireOp",EDGE,"E108.MirrorCS"),sQuery(id+"F8.wireOp",EDGE,"E109.MirrorCS"),sQuery(id+"F8.wireOp",EDGE,"E110.MirrorCS"),sQuery(id+"F8.wireOp",EDGE,"E111.MirrorCS"),sQuery(id+"F8.wireOp",EDGE,"E112.MirrorCS"),sQuery(id+"F8.wireOp",EDGE,"E113.MirrorCS"),sQuery(id+"F8.wireOp",EDGE,"E114.MirrorCS")])],"isStart":true});
            extrude(context, id + "F24", {"entities" : qUnion([Q0]), "operationType" : NewBodyOperationType.REMOVE, "oppositeDirection" : true, "depth" : (getVariable(context, 'WT')) * mm});
        }
        {
            var Q0;
            Q0=makeQuery(id+"F18.opExtrude","CAP_FACE",FACE,{"disambiguationData":[OSD([sQuery(id+"F6.wireOp",EDGE,"E53.0"),sQuery(id+"F6.wireOp",EDGE,"E54.0"),sQuery(id+"F6.wireOp",EDGE,"E56"),sQuery(id+"F6.wireOp",EDGE,"E57"),sQuery(id+"F6.wireOp",EDGE,"E58.0"),sQuery(id+"F6.wireOp",EDGE,"E59.0"),sQuery(id+"F6.wireOp",EDGE,"E60"),sQuery(id+"F6.wireOp",EDGE,"E61"),sQuery(id+"F6.wireOp",EDGE,"E62"),sQuery(id+"F6.wireOp",EDGE,"E63"),sQuery(id+"F6.wireOp",EDGE,"E64"),sQuery(id+"F6.wireOp",EDGE,"E65"),sQuery(id+"F6.wireOp",EDGE,"E69"),sQuery(id+"F6.wireOp",EDGE,"E73"),sQuery(id+"F6.wireOp",EDGE,"E74"),sQuery(id+"F6.wireOp",EDGE,"E75.MirrorCS"),sQuery(id+"F6.wireOp",EDGE,"E76.MirrorCS"),sQuery(id+"F6.wireOp",EDGE,"E78.MirrorCS"),sQuery(id+"F6.wireOp",EDGE,"E79.MirrorCS"),sQuery(id+"F6.wireOp",EDGE,"E80.MirrorCS"),sQuery(id+"F6.wireOp",EDGE,"E81.MirrorCS")])],"isStart":true});
            extrude(context, id + "F25", {"entities" : qUnion([Q0]), "operationType" : NewBodyOperationType.REMOVE, "oppositeDirection" : true, "depth" : (getVariable(context, 'WT')) * mm});
        }
        {
            var Q0;
            {var subQ0=sQuery(id+"F14.wireOp",EDGE,"E150.2");Q0=makeQuery(id+"F14.imprint","IMPRINT",FACE,{"disambiguationData":[TD([[makeQuery(id+"F14.imprint","IMPRINT",EDGE,{"derivedFrom":subQ0}),1.0]])]});}
            var Q1;
            {var subQ4=sQuery(id+"F14.wireOp",EDGE,"E146.0");Q1=makeQuery(id+"F14.imprint","IMPRINT",FACE,{"disambiguationData":[TD([[makeQuery(id+"F14.imprint","IMPRINT",EDGE,{"derivedFrom":subQ4}),1.0]])]});}
            var Q2;
            {var subQ1=sQuery(id+"F14.wireOp",EDGE,"E148");Q2=makeQuery(id+"F14.imprint","IMPRINT",FACE,{"disambiguationData":[TD([[makeQuery(id+"F14.imprint","IMPRINT",EDGE,{"derivedFrom":subQ1}),-1.0]])]});}
            var Q3;
            {var subQ0=sQuery(id+"F14.wireOp",EDGE,"E150.0");Q3=makeQuery(id+"F14.imprint","IMPRINT",FACE,{"disambiguationData":[TD([[makeQuery(id+"F14.imprint","IMPRINT",EDGE,{"derivedFrom":subQ0}),-1.0]])]});}
            extrude(context, id + "F26", {"entities" : qUnion([Q0, Q1, Q2, Q3]), "operationType" : NewBodyOperationType.REMOVE, "depth" : (getVariable(context, 'WT')) * mm});
        }
        {
            var Q0;
            Q0=makeQuery(id+"F19.opExtrude","CAP_FACE",FACE,{"disambiguationData":[OSD([sQuery(id+"F4.wireOp",EDGE,"E21.0"),sQuery(id+"F4.wireOp",EDGE,"E23"),sQuery(id+"F4.wireOp",EDGE,"E28"),sQuery(id+"F4.wireOp",EDGE,"E29.0"),sQuery(id+"F4.wireOp",EDGE,"E29.1"),sQuery(id+"F4.wireOp",EDGE,"E29.2"),sQuery(id+"F4.wireOp",EDGE,"E38"),sQuery(id+"F4.wireOp",EDGE,"E39"),sQuery(id+"F4.wireOp",EDGE,"E40.MirrorCS"),sQuery(id+"F4.wireOp",EDGE,"E41.MirrorCS"),sQuery(id+"F4.wireOp",EDGE,"E42.MirrorCS"),sQuery(id+"F4.wireOp",EDGE,"E43.MirrorCS"),sQuery(id+"F4.wireOp",EDGE,"E44.MirrorCS"),sQuery(id+"F4.wireOp",EDGE,"E45.MirrorCS"),sQuery(id+"F4.wireOp",EDGE,"E52")])],"isStart":false});
            extrude(context, id + "F27", {"entities" : qUnion([Q0]), "operationType" : NewBodyOperationType.REMOVE, "oppositeDirection" : true, "depth" : (getVariable(context, 'WT')) * mm});
        }
    });
